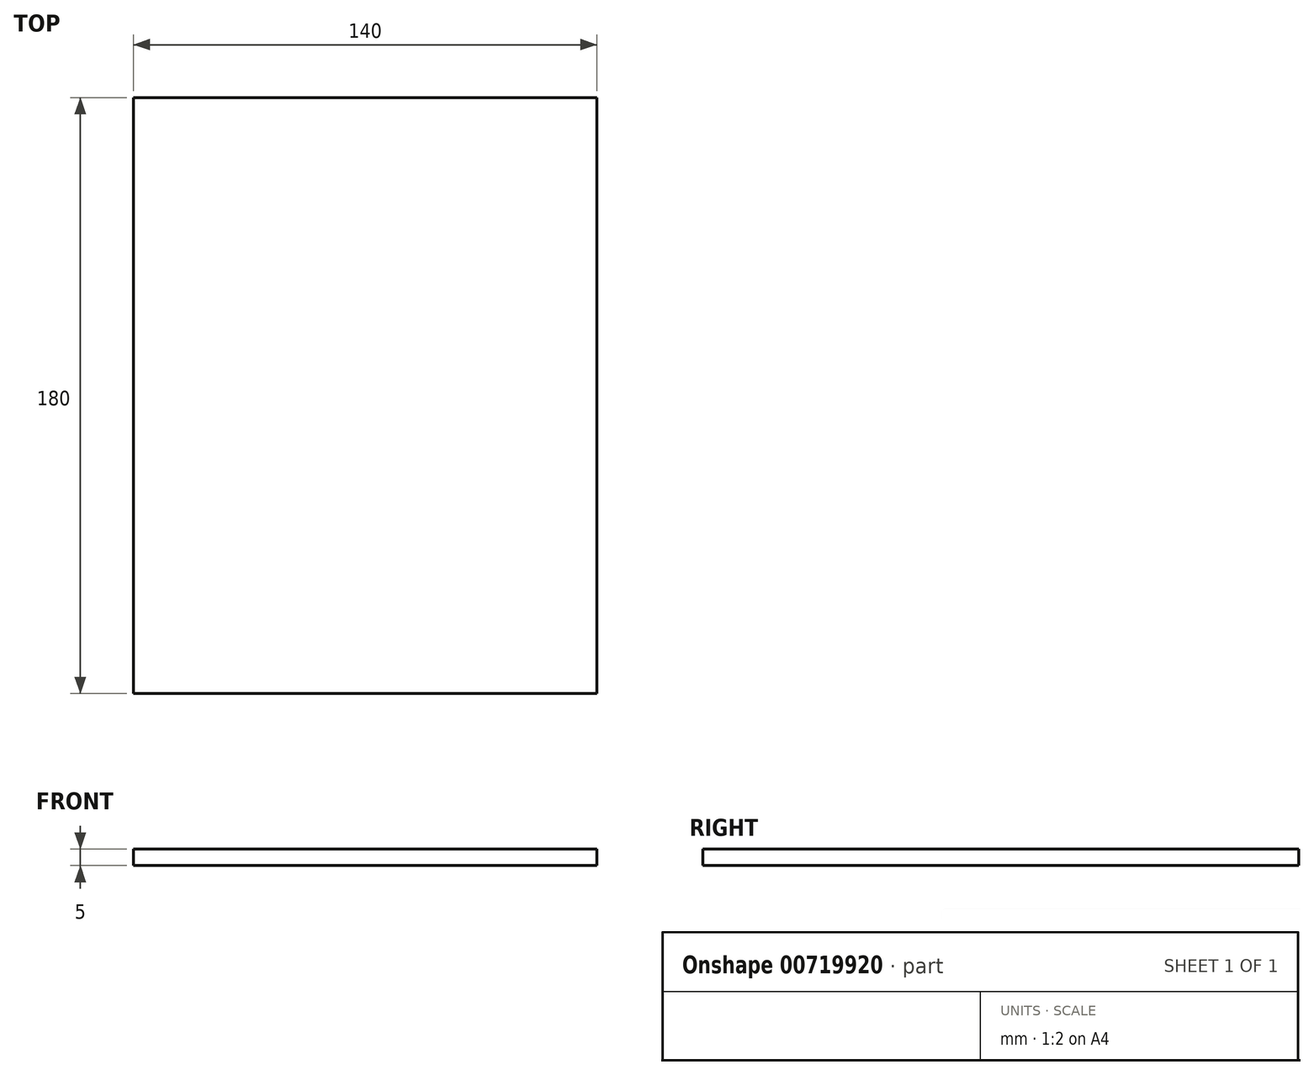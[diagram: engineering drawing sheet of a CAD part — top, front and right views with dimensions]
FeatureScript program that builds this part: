
annotation { "Feature Type Name" : "Feature", "Feature Type Description" : "" }
export const myFeature = defineFeature(function(context is Context, id is Id, definition is map)
    precondition{}
    {
        {
            var Q0;
            Q0=qCreatedBy(makeId("Top.planeOp"),FACE);
            var sketch = newSketch(context, id + "F0", { "sketchPlane" : qUnion([Q0])});
            skLineSegment(sketch, "E0.bottom", {"start": v(0, 0) * mm, "end": v(140, 0) * mm});
            skLineSegment(sketch, "E0.top", {"start": v(0, -180) * mm, "end": v(140, -180) * mm});
            skLineSegment(sketch, "E0.left", {"start": v(0, 0) * mm, "end": v(0, -180) * mm});
            skLineSegment(sketch, "E0.right", {"start": v(140, 0) * mm, "end": v(140, -180) * mm});
            skSolve(sketch);
        }
        {
            var Q0;
            Q0 = qSketchRegion(id + "F0", true);
            extrude(context, id + "F1", {"entities" : qUnion([Q0]), "depth" : 5 * mm, "offsetDistance" : 25 * mm});
        }
    });
